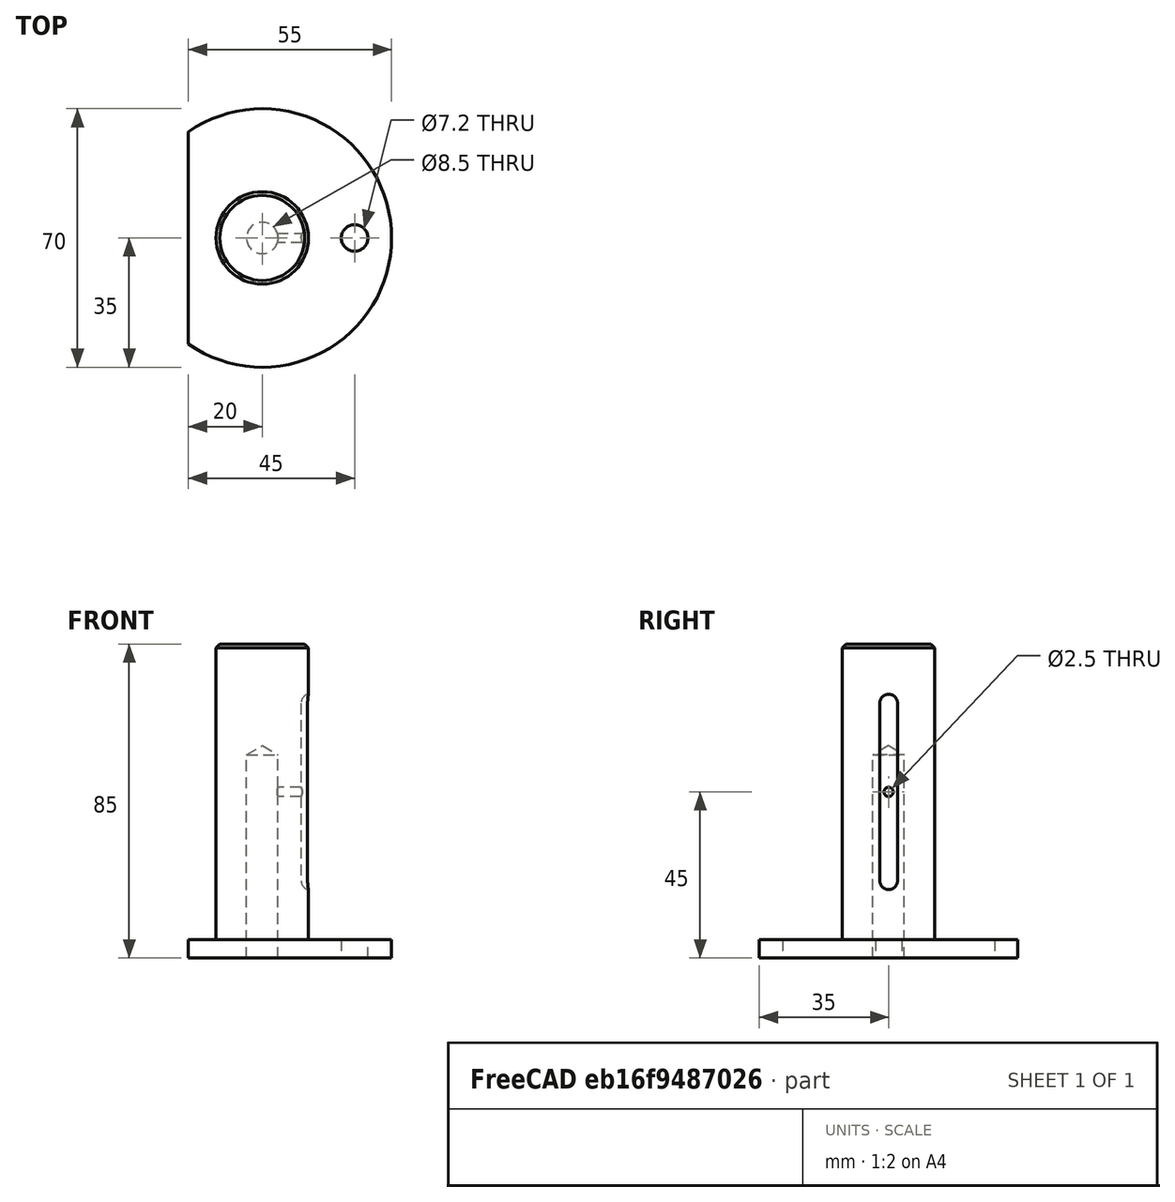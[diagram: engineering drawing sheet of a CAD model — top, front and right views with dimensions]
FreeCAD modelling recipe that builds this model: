
FCSTD DOCUMENT  (FreeCAD 0.20R29177 +426 (Git))
Label: hovairGuidageAxe
License: All rights reserved
LicenseURL: http://en.wikipedia.org/wiki/All_rights_reserved
objects: TechDraw::DrawViewDimension×17, Sketcher::SketchObject×7, TechDraw::DrawViewAnnotation×6, TechDraw::DrawLeaderLine×5, TechDraw::DrawViewBalloon×4, PartDesign::Pocket×3, TechDraw::DrawProjGroupItem×3, PartDesign::Pad×2, PartDesign::Plane×2, TechDraw::DrawSVGTemplate×2, PartDesign::Body×2, TechDraw::DrawViewSection×2, TechDraw::DrawProjGroup×2, TechDraw::DrawPage×2, PartDesign::Line×1, PartDesign::Groove×1, PartDesign::Hole×1, PartDesign::Chamfer×1, PartDesign::FeatureBase×1
note: 29 computed .brp shape members not serialized (recipe doc carries the construction recipe); baked Part::Feature solids carry a one-line shape summary decoded from their .brp

FEATURE [Sketcher::SketchObject] Sketch
  FullyConstrained = true
  MapMode = 5
  Support = -> [XY_Plane]
  sketch-geometry (1):
    g0: Circle CenterX=0 CenterY=0 CenterZ=0 NormalX=0 NormalY=0 NormalZ=1 AngleXU=0 Radius=35
  constraints (2):
    c: Coincident(g0,g-1)
    c: Diameter(g0) = 70
FEATURE [PartDesign::Pad] Pad  label="socle"
  Direction = (0,0,1)
  Length = 5
  Length2 = 10
  Profile = -> Sketch
  ReferenceAxis = -> Sketch [N_Axis]
  Type = 0
FEATURE [Sketcher::SketchObject] Sketch001
  FullyConstrained = true
  MapMode = 5
  Placement = pos=(0,0,5) rot=(0,0,1;0rad)
  Support = -> [Pad]
  sketch-geometry (1):
    g0: Circle CenterX=0 CenterY=0 CenterZ=0 NormalX=0 NormalY=0 NormalZ=1 AngleXU=0 Radius=12.5
  constraints (2):
    c: Coincident(g0,g-1)
    c: Diameter(g0) = 25
FEATURE [PartDesign::Pad] Pad001  label="arbre"
  BaseFeature = -> Pad
  Direction = (0,0,1)
  Length = 80
  Length2 = 10
  Profile = -> Sketch001
  ReferenceAxis = -> Sketch001 [N_Axis]
  Type = 0
FEATURE [PartDesign::Plane] DatumPlane
  Length = 87.3478
  MapMode = 3
  Placement = pos=(0,0,0) rot=(1,0,0;1.5708rad)
  ResizeMode = 0
  Support = -> [Pad001]
  Width = 127.527
FEATURE [Sketcher::SketchObject] Sketch002
  FullyConstrained = true
  MapMode = 5
  Placement = pos=(0,0,0) rot=(1,0,0;1.5708rad)
  Support = -> [DatumPlane]
  sketch-geometry (4):
    g0: LineSegment StartX=10.5 StartY=69 StartZ=0 EndX=10.5 EndY=21 EndZ=0
    g1: ArcOfCircle CenterX=13 CenterY=69 CenterZ=0 NormalX=0 NormalY=0 NormalZ=1 AngleXU=0 Radius=2.5 StartAngle=1.5708 EndAngle=3.1416
    g2: ArcOfCircle CenterX=13 CenterY=21 CenterZ=0 NormalX=0 NormalY=0 NormalZ=1 AngleXU=0 Radius=2.5 StartAngle=3.1416 EndAngle=4.71239
    g3: LineSegment StartX=13 StartY=71.5 StartZ=0 EndX=13 EndY=18.5 EndZ=0
  constraints (14):
    c: Vertical(g0)
    c: DistanceY(g0,g0) = 48
    c: Diameter(g1) = 5
    c: Coincident(g1,g0)
    c: Coincident(g2,g0)
    c: Diameter(g2) = 5
    c: Parallel(g0,g3)
    c: DistanceY(g3,g3) = 53
    c: Coincident(g1,g3)
    c: PointOnObject(g1,g3)
    c: Coincident(g2,g3)
    c: DistanceX(g0,g1) = 2.5
    c: DistanceY(g-1,g2) = 21
    c: DistanceX(g-1,g2) = 13
FEATURE [PartDesign::Line] DatumLine
  AttacherType = Attacher::AttachEngineLine
  Length = 20
  MapMode = 29
  Placement = pos=(13,0,0) rot=(0,1,0;3.14159rad)
  ResizeMode = 0
  Support = -> [Sketch002]
FEATURE [PartDesign::Groove] Groove  label="rainure"
  Angle = 360
  Axis = (0,-2e-16,-1)
  Base = (13,0,0)
  BaseFeature = -> Pad001
  Profile = -> Sketch002
  ReferenceAxis = -> DatumLine
FEATURE [PartDesign::Plane] DatumPlane001
  Length = 87.4488
  MapMode = 4
  Placement = pos=(0,0,0) rot=(0.57735,0.57735,0.57735;2.0944rad)
  ResizeMode = 0
  Support = -> [Pad001]
  Width = 127.539
FEATURE [Sketcher::SketchObject] Sketch003
  FullyConstrained = true
  MapMode = 5
  Placement = pos=(0,0,0) rot=(0.57735,0.57735,0.57735;2.0944rad)
  Support = -> [DatumPlane001]
  sketch-geometry (1):
    g0: Circle CenterX=0 CenterY=45 CenterZ=0 NormalX=0 NormalY=0 NormalZ=1 AngleXU=0 Radius=1.25
  constraints (3):
    c: DistanceY(g-1,g0) = 45
    c: DistanceX(g-1,g0) = 0
    c: Diameter(g0) = 2.5
FEATURE [PartDesign::Pocket] Pocket  label="canal"
  BaseFeature = -> Groove
  Direction = (-1,0,0)
  Length = 5
  Length2 = 5
  Profile = -> Sketch003
  ReferenceAxis = -> Sketch003 [N_Axis]
  Reversed = true
  Type = 1
FEATURE [Sketcher::SketchObject] Sketch004
  FullyConstrained = true
  MapMode = 5
  Placement = pos=(0,0,0) rot=(1,0,0;3.14159rad)
  Support = -> [Pocket]
  sketch-geometry (1):
    g0: Circle CenterX=25 CenterY=0 CenterZ=0 NormalX=0 NormalY=0 NormalZ=1 AngleXU=0 Radius=3.6
  constraints (3):
    c: PointOnObject(g0,g-1)
    c: DistanceX(g-1,g0) = 25
    c: Diameter(g0) = 7.2
FEATURE [PartDesign::Pocket] Pocket001  label="trouDeFixation"
  BaseFeature = -> Pocket
  Direction = (0,0,1)
  Length = 5
  Length2 = 5
  Profile = -> Sketch004
  ReferenceAxis = -> Sketch004 [N_Axis]
  Type = 1
FEATURE [Sketcher::SketchObject] Sketch005
  FullyConstrained = false
  MapMode = 5
  Placement = pos=(0,0,0) rot=(1,0,0;3.14159rad)
  Support = -> [Pocket001]
  sketch-geometry (1):
    g0: Circle CenterX=0 CenterY=0 CenterZ=0 NormalX=0 NormalY=0 NormalZ=1 AngleXU=0 Radius=12.5084
  constraints (1):
    c: Coincident(g0,g-1)
FEATURE [PartDesign::Hole] Hole
  BaseFeature = -> Pocket001
  CustomThreadClearance = 0
  Depth = 55
  DepthType = 0
  Diameter = 8.5
  DrillForDepth = false
  DrillPoint = 1
  DrillPointAngle = 118
  HoleCutCountersinkAngle = 90
  HoleCutCustomValues = false
  HoleCutDepth = 0
  HoleCutDiameter = 11.1
  HoleCutType = 0
  ModelThread = false
  Profile = -> Sketch005
  Tapered = false
  TaperedAngle = 90
  ThreadClass = 0
  ThreadDepth = 55
  ThreadDepthType = 0
  ThreadDirection = 0
  ThreadFit = 0
  ThreadSize = 18
  ThreadType = 1
  Threaded = true
  UseCustomThreadClearance = false
FEATURE [TechDraw::DrawSVGTemplate] Template
  EditableTexts = Designed_by_Name=Designed by Name; Drawing_number=Drawing number; FC-Date=Date; FC-SC=Scale; FC-SH=Sheet; FC-Title=Title; Subtitle=Subtitle; Weight=Weight
  Height = 210
  Orientation = 1
  Width = 297
FEATURE [PartDesign::Chamfer] Chamfer
  Angle = 45
  Base = -> Hole [Edge17]
  BaseFeature = -> Hole
  ChamferType = 0
  FlipDirection = false
  Size = 1
  Size2 = 1
  SupportTransform = false
  UseAllEdges = false
FEATURE [PartDesign::Body] Body  label="axe"
  Group = -> [Sketch,Pad,Sketch001,Pad001,DatumPlane,Sketch002,DatumLine,Groove,DatumPlane001,Sketch003,Pocket,Sketch004,Pocket001,Sketch005,Hole,Chamfer]
  Origin = -> Origin
  Tip = -> Chamfer
FEATURE [TechDraw::DrawProjGroupItem] ProjItem  label="Front"
  CoarseView = false
  Direction = (0,0,1)
  Focus = 100
  HardHidden = true
  IsoCount = 0
  IsoHidden = false
  IsoVisible = true
  LockPosition = true
  Perspective = false
  Rotation = 0
  RotationVector = (0,-1,0)
  ScaleType = 2
  SeamHidden = false
  SeamVisible = true
  SmoothHidden = false
  SmoothVisible = true
  Source = -> [Chamfer]
  Type = 0
  X = 0
  XDirection = (0,-1,0)
  Y = 0
FEATURE [TechDraw::DrawViewSection] SectionView
  BaseView = -> ProjItem
  CoarseView = false
  CutSurfaceDisplay = 2
  Direction = (0,-1,0)
  FileGeomPattern = <userpath>/AppData/Local/Programs/FreeCAD 0.20/data/Mod/TechDraw/PAT/FCPAT.pat
  FileHatchPattern = <userpath>/AppData/Local/Programs/FreeCAD 0.20/data/Mod/TechDraw/Patterns/simple.svg
  Focus = 100
  FuseBeforeCut = false
  HardHidden = false
  HatchScale = 1
  IsoCount = 0
  IsoHidden = false
  IsoVisible = true
  LockPosition = true
  NameGeomPattern = Diamant
  Perspective = false
  Rotation = 0
  ScaleType = 2
  SeamHidden = false
  SeamVisible = true
  SectionDirection = 1
  SectionNormal = (0,-1,0)
  SectionOrigin = (0.025,0,42.51)
  SectionSymbol = A
  SmoothHidden = false
  SmoothVisible = true
  Source = -> [Chamfer]
  X = 145.231
  XDirection = (0,0,-1)
  Y = 125.088
FEATURE [TechDraw::DrawViewSection] SectionView001
  BaseView = -> SectionView
  CoarseView = false
  CutSurfaceDisplay = 2
  Direction = (0,0,-1)
  FileGeomPattern = <userpath>/AppData/Local/Programs/FreeCAD 0.20/data/Mod/TechDraw/PAT/FCPAT.pat
  FileHatchPattern = <userpath>/AppData/Local/Programs/FreeCAD 0.20/data/Mod/TechDraw/Patterns/simple.svg
  Focus = 100
  FuseBeforeCut = false
  HardHidden = false
  HatchScale = 1
  IsoCount = 0
  IsoHidden = false
  IsoVisible = true
  LockPosition = true
  NameGeomPattern = Diamant
  Perspective = false
  Rotation = 0
  ScaleType = 2
  SeamHidden = false
  SeamVisible = true
  SectionDirection = 1
  SectionNormal = (0,0,-1)
  SectionOrigin = (0,17.5,45)
  SectionSymbol = B
  SmoothHidden = false
  SmoothVisible = true
  Source = -> [Chamfer]
  X = 45.6336
  XDirection = (0,1,0)
  Y = 125.088
FEATURE [PartDesign::FeatureBase] Clone
  BaseFeature = -> Body
FEATURE [Sketcher::SketchObject] Sketch006
  FullyConstrained = false
  MapMode = 5
  Placement = pos=(0,0,5) rot=(0,0,1;0rad)
  Support = -> [Clone]
  sketch-geometry (4):
    g0: LineSegment StartX=-45.8649 StartY=37.2212 StartZ=0 EndX=-20 EndY=37.2212 EndZ=0
    g1: LineSegment StartX=-20 StartY=37.2212 StartZ=0 EndX=-20 EndY=-43.7351 EndZ=0
    g2: LineSegment StartX=-20 StartY=-43.7351 StartZ=0 EndX=-45.8649 EndY=-43.7351 EndZ=0
    g3: LineSegment StartX=-45.8649 StartY=-43.7351 StartZ=0 EndX=-45.8649 EndY=37.2212 EndZ=0
  constraints (9):
    c: Coincident(g0,g1)
    c: Coincident(g1,g2)
    c: Coincident(g2,g3)
    c: Coincident(g3,g0)
    c: Horizontal(g0)
    c: Horizontal(g2)
    c: Vertical(g1)
    c: Vertical(g3)
    c: DistanceX(g0,g-1) = 20
FEATURE [PartDesign::Pocket] Pocket002
  BaseFeature = -> Clone
  Direction = (0,0,-1)
  Length = 5
  Length2 = 5
  Profile = -> Sketch006
  ReferenceAxis = -> Sketch006 [N_Axis]
  Type = 1
FEATURE [PartDesign::Body] Body001  label="axeCoupé"
  BaseFeature = -> Body
  Group = -> [Clone,Sketch006,Pocket002]
  Origin = -> Origin001
  Tip = -> Pocket002
FEATURE [TechDraw::DrawLeaderLine] LeaderLine
  AutoHorizontal = false
  EndSymbol = 7
  LeaderParent = -> SectionView
  LockPosition = true
  Rotation = 0
  Scalable = false
  ScaleType = 0
  StartSymbol = 0
  WayPoints = (2) [(0,0,0),(107.71,0,0)]
  X = -2.58379
  Y = 30.059
FEATURE [TechDraw::DrawLeaderLine] LeaderLine001
  AutoHorizontal = true
  EndSymbol = 7
  LeaderParent = -> SectionView
  LockPosition = true
  Rotation = 0
  Scalable = false
  ScaleType = 0
  StartSymbol = 0
  WayPoints = (2) [(0,0,0),(105.993,0,0)]
  X = -2.56286
  Y = -30.0156
FEATURE [TechDraw::DrawLeaderLine] LeaderLine002
  AutoHorizontal = true
  EndSymbol = 7
  LeaderParent = -> SectionView
  LockPosition = true
  Rotation = 0
  Scalable = false
  ScaleType = 0
  StartSymbol = 7
  WayPoints = (2) [(0,0,0),(0,0,0)]
  X = -2.53021
  Y = 29.868
FEATURE [TechDraw::DrawLeaderLine] LeaderLine003
  AutoHorizontal = false
  EndSymbol = 7
  LeaderParent = -> SectionView
  LockPosition = true
  Rotation = 0
  Scalable = false
  ScaleType = 0
  StartSymbol = 7
  WayPoints = (2) [(0,0,0),(-0.132979,602.237,0)]
  X = -2.47667
  Y = 30.1033
FEATURE [TechDraw::DrawViewAnnotation] Annotation
  Font = osifont
  LineSpace = 80
  LockPosition = false
  MaxWidth = -1
  Rotation = 0
  ScaleType = 0
  Text = B
  TextSize = 5
  TextStyle = 0
  X = 150.253
  Y = 100.234
FEATURE [TechDraw::DrawViewAnnotation] Annotation001
  Font = osifont
  LineSpace = 80
  LockPosition = false
  MaxWidth = -1
  Rotation = 0
  ScaleType = 0
  Text = B
  TextSize = 5
  TextStyle = 0
  X = 128.731
  Y = 154.896
FEATURE [TechDraw::DrawViewDimension] Dimension
  AngleOverride = false
  Arbitrary = false
  ArbitraryTolerances = false
  EqualTolerance = true
  ExtensionAngle = 0
  FormatSpec = %.2w
  FormatSpecOverTolerance = %+.2w
  FormatSpecUnderTolerance = %+.2w
  Inverted = false
  LineAngle = 0
  LockPosition = false
  MeasureType = 1
  OverTolerance = 0
  References2D = -> [ProjItem]
  Rotation = 0
  ScaleType = 0
  TheoreticalExact = false
  Type = 2
  UnderTolerance = 0
  X = 36.9797
  Y = 14.9752
FEATURE [TechDraw::DrawViewDimension] Dimension001
  AngleOverride = false
  Arbitrary = false
  ArbitraryTolerances = false
  EqualTolerance = true
  ExtensionAngle = 0
  FormatSpec = ⌀%.2w
  FormatSpecOverTolerance = %+.2w
  FormatSpecUnderTolerance = %+.2w
  Inverted = false
  LineAngle = 0
  LockPosition = false
  MeasureType = 1
  OverTolerance = 0
  References2D = -> [ProjItem]
  Rotation = 0
  ScaleType = 0
  TheoreticalExact = false
  Type = 5
  UnderTolerance = 0
  X = -13.1595
  Y = 50.4723
FEATURE [TechDraw::DrawLeaderLine] LeaderLine004
  AutoHorizontal = false
  EndSymbol = 7
  LeaderParent = -> SectionView
  LockPosition = true
  Rotation = 0
  Scalable = false
  ScaleType = 0
  StartSymbol = 7
  WayPoints = (4) [(0,0,0),(-301.398,0.387401,0),(-302.948,100.337,0),(0,100.337,0)]
  X = 42.5614
  Y = 5.06396
FEATURE [TechDraw::DrawViewDimension] Dimension003
  AngleOverride = false
  Arbitrary = true
  ArbitraryTolerances = false
  EqualTolerance = true
  ExtensionAngle = 0
  FormatSpec = M10
  FormatSpecOverTolerance = %+.2w
  FormatSpecUnderTolerance = %+.2w
  Inverted = false
  LineAngle = 0
  LockPosition = false
  MeasureType = 1
  OverTolerance = 0
  References2D = -> [SectionView]
  Rotation = 0
  ScaleType = 0
  TheoreticalExact = false
  Type = 2
  UnderTolerance = 0
  X = 49.2963
  Y = -10.293
FEATURE [TechDraw::DrawViewDimension] Dimension002
  AngleOverride = false
  Arbitrary = false
  ArbitraryTolerances = false
  EqualTolerance = true
  ExtensionAngle = 0
  FormatSpec = %.2w
  FormatSpecOverTolerance = %+.2w
  FormatSpecUnderTolerance = %+.2w
  Inverted = false
  LineAngle = 0
  LockPosition = false
  MeasureType = 1
  OverTolerance = 0
  References2D = -> [SectionView]
  Rotation = 0
  ScaleType = 0
  TheoreticalExact = false
  Type = 2
  UnderTolerance = 0
  X = 56.2924
  Y = 1.90033
FEATURE [TechDraw::DrawViewDimension] Dimension004
  AngleOverride = false
  Arbitrary = false
  ArbitraryTolerances = false
  EqualTolerance = false
  ExtensionAngle = 0
  FormatSpec = %.2w
  FormatSpecOverTolerance = %+.2w
  FormatSpecUnderTolerance = %+.2w
  Inverted = false
  LineAngle = 0
  LockPosition = false
  MeasureType = 1
  OverTolerance = 0
  References2D = -> [SectionView]
  Rotation = 0
  ScaleType = 0
  TheoreticalExact = false
  Type = 2
  UnderTolerance = -0.05
  X = -63.0676
  Y = 1.74324
FEATURE [TechDraw::DrawViewDimension] Dimension005
  AngleOverride = false
  Arbitrary = false
  ArbitraryTolerances = false
  EqualTolerance = true
  ExtensionAngle = 0
  FormatSpec = %.2w x45°
  FormatSpecOverTolerance = %+.2w
  FormatSpecUnderTolerance = %+.2w
  Inverted = false
  LineAngle = 0
  LockPosition = false
  MeasureType = 1
  OverTolerance = 0
  References2D = -> [SectionView]
  Rotation = 0
  ScaleType = 0
  TheoreticalExact = false
  Type = 1
  UnderTolerance = 0
  X = -52.2898
  Y = 41.53
FEATURE [TechDraw::DrawViewBalloon] Balloon
  BubbleShape = 7
  EndType = 7
  EndTypeScale = 1
  KinkLength = 5
  LockPosition = false
  OriginX = 37.1194
  OriginY = -22.8833
  Rotation = 0
  ScaleType = 0
  ShapeScale = 1
  SourceView = -> SectionView
  Text = 3,2
  TextWrapLen = -1
  X = 25.6235
  Y = -15.4237
FEATURE [TechDraw::DrawViewBalloon] Balloon001
  BubbleShape = 6
  EndType = 0
  EndTypeScale = 1
  KinkLength = 5
  LockPosition = false
  OriginX = -47.6881
  OriginY = 0.0800074
  Rotation = 0
  ScaleType = 0
  ShapeScale = 1
  SourceView = -> SectionView
  Text = ⟂|0,05|A
  TextWrapLen = -1
  X = -26.7526
  Y = -32.9986
FEATURE [TechDraw::DrawViewBalloon] Balloon003
  BubbleShape = 6
  EndType = 6
  EndTypeScale = 1
  KinkLength = 5
  LockPosition = false
  OriginX = 37.6725
  OriginY = -33.4487
  Rotation = 0
  ScaleType = 0
  ShapeScale = 1
  SourceView = -> SectionView
  Text = A
  TextWrapLen = -1
  X = 16.6079
  Y = -33.1243
FEATURE [TechDraw::DrawViewDimension] Dimension006
  AngleOverride = false
  Arbitrary = false
  ArbitraryTolerances = false
  EqualTolerance = true
  ExtensionAngle = 0
  FormatSpec = %.2w
  FormatSpecOverTolerance = %+.2w
  FormatSpecUnderTolerance = %+.2w
  Inverted = false
  LineAngle = 0
  LockPosition = false
  MeasureType = 1
  OverTolerance = 0
  References2D = -> [SectionView]
  Rotation = 0
  ScaleType = 0
  TheoreticalExact = false
  Type = 1
  UnderTolerance = 0
  X = -14.2297
  Y = 44.3108
FEATURE [TechDraw::DrawViewDimension] Dimension007
  AngleOverride = false
  Arbitrary = false
  ArbitraryTolerances = false
  EqualTolerance = true
  ExtensionAngle = 0
  FormatSpec = %.2w
  FormatSpecOverTolerance = %+.2w
  FormatSpecUnderTolerance = %+.2w
  Inverted = false
  LineAngle = 0
  LockPosition = false
  MeasureType = 1
  OverTolerance = 0
  References2D = -> [SectionView]
  Rotation = 0
  ScaleType = 0
  TheoreticalExact = false
  Type = 1
  UnderTolerance = 0
  X = 28.2703
  Y = 44.3108
FEATURE [TechDraw::DrawViewDimension] Dimension008
  AngleOverride = false
  Arbitrary = false
  ArbitraryTolerances = false
  EqualTolerance = true
  ExtensionAngle = 0
  FormatSpec = %.2w
  FormatSpecOverTolerance = %+.2w
  FormatSpecUnderTolerance = %+.2w
  Inverted = false
  LineAngle = 0
  LockPosition = false
  MeasureType = 1
  OverTolerance = 0
  References2D = -> [SectionView]
  Rotation = 0
  ScaleType = 0
  TheoreticalExact = false
  Type = 1
  UnderTolerance = 0
  X = 30.4672
  Y = 52.2793
FEATURE [TechDraw::DrawViewDimension] Dimension009
  AngleOverride = false
  Arbitrary = false
  ArbitraryTolerances = false
  EqualTolerance = true
  ExtensionAngle = 0
  FormatSpec = %.2w
  FormatSpecOverTolerance = %+.2w
  FormatSpecUnderTolerance = %+.2w
  Inverted = false
  LineAngle = 0
  LockPosition = false
  MeasureType = 1
  OverTolerance = 0
  References2D = -> [SectionView]
  Rotation = 0
  ScaleType = 0
  TheoreticalExact = false
  Type = 1
  UnderTolerance = 0
  X = -4.03278
  Y = 52.2793
FEATURE [TechDraw::DrawViewDimension] Dimension010
  AngleOverride = false
  Arbitrary = false
  ArbitraryTolerances = false
  EqualTolerance = true
  ExtensionAngle = 0
  FormatSpec = %.2w
  FormatSpecOverTolerance = %+.2w
  FormatSpecUnderTolerance = %+.2w
  Inverted = false
  LineAngle = 0
  LockPosition = false
  MeasureType = 1
  OverTolerance = 0
  References2D = -> [SectionView]
  Rotation = 0
  ScaleType = 0
  TheoreticalExact = false
  Type = 1
  UnderTolerance = 0
  X = -0.315315
  Y = 60.4347
FEATURE [TechDraw::DrawViewDimension] Dimension011
  AngleOverride = false
  Arbitrary = false
  ArbitraryTolerances = false
  EqualTolerance = true
  ExtensionAngle = 0
  FormatSpec = %.2w
  FormatSpecOverTolerance = %+.2w
  FormatSpecUnderTolerance = %+.2w
  Inverted = false
  LineAngle = 0
  LockPosition = false
  MeasureType = 1
  OverTolerance = 0
  References2D = -> [SectionView]
  Rotation = 0
  ScaleType = 0
  TheoreticalExact = false
  Type = 1
  UnderTolerance = 0
  X = 26.9745
  Y = -38.2583
FEATURE [TechDraw::DrawViewDimension] Dimension012
  AngleOverride = false
  Arbitrary = false
  ArbitraryTolerances = false
  EqualTolerance = true
  ExtensionAngle = 0
  FormatSpec = %.2w
  FormatSpecOverTolerance = %+.2w
  FormatSpecUnderTolerance = %+.2w
  Inverted = false
  LineAngle = 0
  LockPosition = false
  MeasureType = 1
  OverTolerance = 0
  References2D = -> [SectionView]
  Rotation = 0
  ScaleType = 0
  TheoreticalExact = false
  Type = 1
  UnderTolerance = 0
  X = 18.4718
  Y = -46.6468
FEATURE [TechDraw::DrawViewDimension] Dimension013
  AngleOverride = false
  Arbitrary = false
  ArbitraryTolerances = false
  EqualTolerance = true
  ExtensionAngle = 0
  FormatSpec = %.2w
  FormatSpecOverTolerance = %+.2w
  FormatSpecUnderTolerance = %+.2w
  Inverted = false
  LineAngle = 0
  LockPosition = false
  MeasureType = 1
  OverTolerance = 0
  References2D = -> [SectionView]
  Rotation = 0
  ScaleType = 0
  TheoreticalExact = false
  Type = 1
  UnderTolerance = 0
  X = 15
  Y = -57.6346
FEATURE [TechDraw::DrawViewBalloon] Balloon004
  BubbleShape = 7
  EndType = 7
  EndTypeScale = 1
  KinkLength = 5
  LockPosition = false
  OriginX = -51.0195
  OriginY = 13.1064
  Rotation = 0
  ScaleType = 0
  ShapeScale = 1
  SourceView = -> SectionView
  Text = 3.2
  TextWrapLen = -1
  X = -63.8649
  Y = 23.9097
FEATURE [TechDraw::DrawViewDimension] Dimension014
  AngleOverride = false
  Arbitrary = false
  ArbitraryTolerances = false
  EqualTolerance = true
  ExtensionAngle = 0
  FormatSpec = %.2w
  FormatSpecOverTolerance = %+.2w
  FormatSpecUnderTolerance = %+.2w
  Inverted = false
  LineAngle = 0
  LockPosition = false
  MeasureType = 1
  OverTolerance = 0
  References2D = -> [SectionView001]
  Rotation = 0
  ScaleType = 0
  TheoreticalExact = false
  Type = 2
  UnderTolerance = 0
  X = 13.3978
  Y = 22.2477
FEATURE [TechDraw::DrawViewDimension] Dimension015
  AngleOverride = false
  Arbitrary = false
  ArbitraryTolerances = false
  EqualTolerance = true
  ExtensionAngle = 0
  FormatSpec = R%.2w
  FormatSpecOverTolerance = %+.2w
  FormatSpecUnderTolerance = %+.2w
  Inverted = false
  LineAngle = 0
  LockPosition = false
  MeasureType = 1
  OverTolerance = 0
  References2D = -> [SectionView001]
  Rotation = 0
  ScaleType = 0
  TheoreticalExact = false
  Type = 4
  UnderTolerance = 0
  X = -9.47911
  Y = 30.6866
FEATURE [TechDraw::DrawViewAnnotation] Annotation002
  Font = osifont
  LineSpace = 80
  LockPosition = false
  MaxWidth = -1
  Rotation = 0
  ScaleType = 0
  Text = A-A
  TextSize = 8
  TextStyle = 0
  X = 142.454
  Y = 196.062
FEATURE [TechDraw::DrawViewAnnotation] Annotation003
  Font = osifont
  LineSpace = 80
  LockPosition = false
  MaxWidth = -1
  Rotation = 0
  ScaleType = 0
  Text = B-B
  TextSize = 8
  TextStyle = 0
  X = 40.1815
  Y = 194.657
FEATURE [TechDraw::DrawProjGroupItem] ProjItem001  label="FrontTopRight"
  CoarseView = false
  Direction = (0.57735,-0.57735,0.57735)
  Focus = 100
  HardHidden = false
  IsoCount = 0
  IsoHidden = false
  IsoVisible = true
  LockPosition = true
  Perspective = false
  Rotation = 0
  RotationVector = (1,0,0)
  ScaleType = 2
  SeamHidden = false
  SeamVisible = true
  SmoothHidden = false
  SmoothVisible = true
  Source = -> [Chamfer]
  Type = 7
  X = -186.324
  XDirection = (0,-0.707107,-0.707107)
  Y = -66.9498
FEATURE [TechDraw::DrawProjGroup] ProjGroup
  Anchor = -> ProjItem
  AutoDistribute = true
  LockPosition = false
  ProjectionType = 0
  Rotation = 0
  ScaleType = 0
  Source = -> [Chamfer]
  Views = -> [ProjItem,ProjItem001]
  X = 244.022
  Y = 125.088
  spacingX = 15
  spacingY = 15
FEATURE [TechDraw::DrawViewAnnotation] Annotation004
  Font = osifont
  LineSpace = 80
  LockPosition = false
  MaxWidth = -1
  Rotation = 0
  ScaleType = 0
  Text = VUE ISO
  TextSize = 8
  TextStyle = 0
  X = 60.6275
  Y = 23.3449
FEATURE [TechDraw::DrawPage] Page  label="Axe"
  KeepUpdated = true
  NextBalloonIndex = 6
  ProjectionType = 0
  Template = -> Template
  Views = -> [ProjGroup,SectionView,SectionView001,LeaderLine,LeaderLine001,LeaderLine002,LeaderLine003,Annotation,Annotation001,Dimension,Dimension001,LeaderLine004,Dimension002,Dimension003,Dimension004,Dimension005,Balloon,Balloon001,Balloon003,Dimension006,Dimension007,Dimension008,Dimension009,Dimension010,Dimension011,Dimension012,Dimension013,Balloon004,Dimension014,Dimension015,Annotation002,+2 more]
FEATURE [TechDraw::DrawSVGTemplate] Template001
  EditableTexts = Designed_by_Name=Designed by Name; Drawing_number=Drawing number; FC-Date=Date; FC-SC=Scale; FC-SH=Sheet; FC-Title=Title; Subtitle=Subtitle; Weight=Weight
  Height = 210
  Orientation = 1
  Width = 297
FEATURE [TechDraw::DrawProjGroupItem] ProjItem002  label="Front001"
  CoarseView = false
  Direction = (0,0,1)
  Focus = 100
  HardHidden = false
  IsoCount = 0
  IsoHidden = false
  IsoVisible = true
  LockPosition = true
  Perspective = false
  Rotation = 0
  RotationVector = (-1,0,0)
  ScaleType = 2
  SeamHidden = false
  SeamVisible = true
  SmoothHidden = false
  SmoothVisible = true
  Source = -> [Pocket002]
  Type = 0
  X = 0
  XDirection = (-1e-16,-1,0)
  Y = 0
FEATURE [TechDraw::DrawProjGroup] ProjGroup001
  Anchor = -> ProjItem002
  AutoDistribute = true
  LockPosition = false
  ProjectionType = 0
  Rotation = 0
  ScaleType = 0
  Source = -> [Pocket002]
  Views = -> [ProjItem002]
  X = 134.173
  Y = 158.626
  spacingX = 15
  spacingY = 15
FEATURE [TechDraw::DrawViewDimension] Dimension016
  AngleOverride = false
  Arbitrary = false
  ArbitraryTolerances = false
  EqualTolerance = true
  ExtensionAngle = 0
  FormatSpec = %.2w
  FormatSpecOverTolerance = %+.2w
  FormatSpecUnderTolerance = %+.2w
  Inverted = false
  LineAngle = 0
  LockPosition = false
  MeasureType = 1
  OverTolerance = 0
  References2D = -> [ProjItem002]
  Rotation = 0
  ScaleType = 0
  TheoreticalExact = false
  Type = 2
  UnderTolerance = 0
  X = 63.0749
  Y = -15
FEATURE [TechDraw::DrawViewAnnotation] Annotation005
  Font = osifont
  LineSpace = 80
  LockPosition = false
  MaxWidth = -1
  Rotation = 0
  ScaleType = 0
  Text = L'axe coupé est entièrement identique à l'axe normal, | exepté la partie coupé (seul côte de ce dessin)
  TextSize = 8
  TextStyle = 0
  X = 144.816
  Y = 96.8129
FEATURE [TechDraw::DrawPage] Page001  label="AxeCoupé"
  KeepUpdated = true
  NextBalloonIndex = 1
  ProjectionType = 0
  Template = -> Template001
  Views = -> [ProjGroup001,Dimension016,Annotation005]
